# Revit family: Ø2450mm-TIPO A - con y sin HDPE - copia
name_source: partatom
category: Modelos genéricos
units: mm (PartAtom-declared; Revit-internal decimal feet)

## family parameters
Compartido = No
Corte con vacíos al cargar = No
Cota de conector redondo = Diámetro de uso
Puede alojar armadura = No
Punto de cálculo de habitación = No
Se basa en plano de trabajo = No
Siempre vertical = Sí
Tipo de pieza = Normal

## types (1)
- Ø2450mm-TIPO A - con y sin HDPE - copia
    Comentarios de tipo = CLASE 2,3,4 Y 5
    Descripción = TUBO JACKING PIPE Ø200cm-TIPO A
    Diametro externo = 2850 mm
    Diametro interno = 2450 mm  [stored 8.03806 ft]
    Elevación por defecto = 0 mm  [stored 0 ft]
    Espesor muro = 200 mm  [stored 0.656168 ft]
    Fabricante = TITAN
    Largo = 2500 mm  [stored 8.2021 ft]
    Radio = 1225 mm  [stored 4.01903 ft]
    URL = www.titancemento.com

note: [stored X ft] marks values corroborated as IEEE doubles in the binary element streams (Revit-internal decimal feet)
